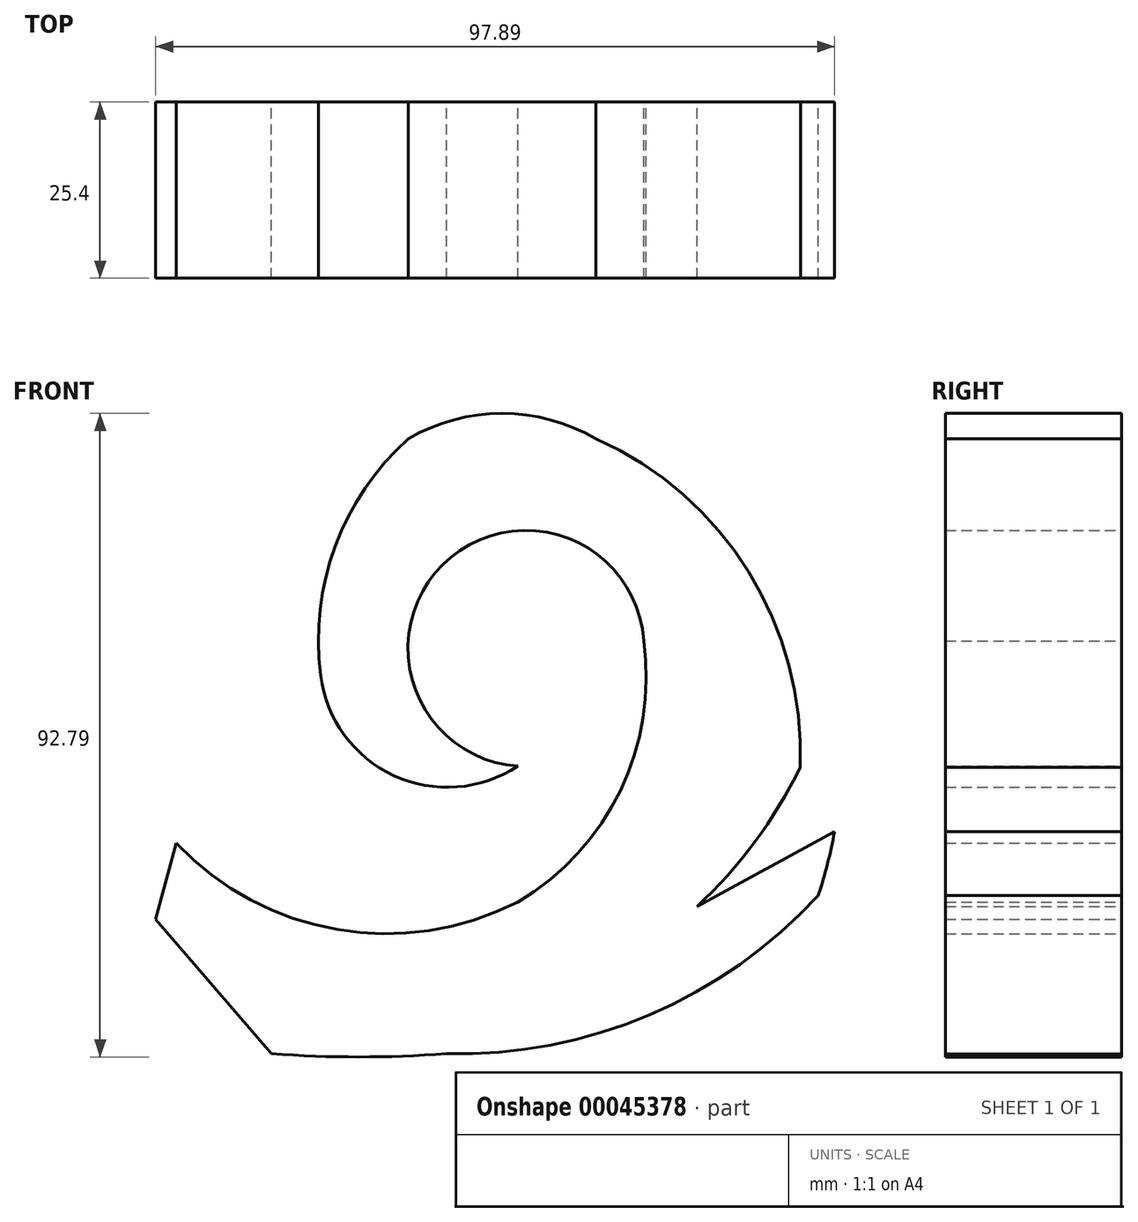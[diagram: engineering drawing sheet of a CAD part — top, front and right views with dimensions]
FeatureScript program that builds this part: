
annotation { "Feature Type Name" : "Feature", "Feature Type Description" : "" }
export const myFeature = defineFeature(function(context is Context, id is Id, definition is map)
    precondition{}
    {
        {
            var Q0;
            Q0=qCreatedBy(makeId("Front.planeOp"),FACE);
            var sketch = newSketch(context, id + "F0", { "sketchPlane" : qUnion([Q0])});
            skArc(sketch, "E0", {"start": v(-28.45, -4.94) * mm, "mid": v(-17.88, -19.42) * mm, "end": v(0, -18.06) * mm});
            skArc(sketch, "E1", {"start": v(18.16, 0) * mm, "mid": v(-10.82, 10.99) * mm, "end": v(0, -18.06) * mm});
            skArc(sketch, "E2", {"start": v(-15.78, 29.16) * mm, "mid": v(-26.32, 13.67) * mm, "end": v(-28.45, -4.94) * mm});
            skArc(sketch, "E3", {"start": v(11.26, 29.16) * mm, "mid": v(-2.26, 32.8) * mm, "end": v(-15.78, 29.16) * mm});
            skArc(sketch, "E4", {"start": v(40.72, -18.26) * mm, "mid": v(33.3, 9.99) * mm, "end": v(11.26, 29.16) * mm});
            skArc(sketch, "E5", {"start": v(0, -37.64) * mm, "mid": v(14.8, -21.57) * mm, "end": v(18.16, 0) * mm});
            skArc(sketch, "E6", {"start": v(10.25, -49.14) * mm, "mid": v(28.02, -36.2) * mm, "end": v(40.72, -18.26) * mm});
            skArc(sketch, "E7", {"start": v(-49.23, -29.16) * mm, "mid": v(-26.03, -41.61) * mm, "end": v(0, -37.64) * mm});
            skArc(sketch, "E8", {"start": v(-35.52, -51.16) * mm, "mid": v(-12.57, -51.62) * mm, "end": v(10.25, -49.14) * mm});
            skLineSegment(sketch, "E9", {"start": v(0, -18.06) * mm, "end": v(0, -23.74) * mm});
            skArc(sketch, "E10", {"start": v(-39.51, -10.04) * mm, "mid": v(-22.53, -24.85) * mm, "end": v(0, -25.45) * mm});
            skArc(sketch, "E11", {"start": v(-34.16, 22.74) * mm, "mid": v(-42.14, 7.21) * mm, "end": v(-39.51, -10.04) * mm});
            skArc(sketch, "E12", {"start": v(2.68, 38.83) * mm, "mid": v(-17.1, 33.9) * mm, "end": v(-34.16, 22.74) * mm});
            skArc(sketch, "E13", {"start": v(40.55, 12.93) * mm, "mid": v(24.95, 30.76) * mm, "end": v(2.68, 38.83) * mm});
            skArc(sketch, "E14", {"start": v(43.33, -36.7) * mm, "mid": v(46.66, -11.62) * mm, "end": v(40.55, 12.93) * mm});
            skArc(sketch, "E15", {"start": v(-10.29, -59.53) * mm, "mid": v(19, -53.93) * mm, "end": v(43.33, -36.7) * mm});
            skArc(sketch, "E16", {"start": v(-35.52, -59.53) * mm, "mid": v(-22.9, -59.99) * mm, "end": v(-10.29, -59.53) * mm});
            skLineSegment(sketch, "E17", {"start": v(-49.23, -29.16) * mm, "end": v(-34.05, -51.28) * mm});
            skLineSegment(sketch, "E18", {"start": v(-34.05, -51.28) * mm, "end": v(-34.05, -59.53) * mm});
            skLineSegment(sketch, "E19", {"start": v(-49.23, -29.16) * mm, "end": v(-52.21, -40.17) * mm});
            skLineSegment(sketch, "E20", {"start": v(-52.21, -40.17) * mm, "end": v(-35.52, -59.53) * mm});
            skLineSegment(sketch, "E21", {"start": v(74.96, -40.28) * mm, "end": v(25.84, -38.3) * mm});
            skLineSegment(sketch, "E22", {"start": v(25.84, -38.3) * mm, "end": v(52.96, -23.52) * mm});
            skLineSegment(sketch, "E23", {"start": v(52.96, -23.52) * mm, "end": v(65.7, -22.46) * mm});
            skSolve(sketch);
        }
        {
            var Q0;
            Q0 = qSketchRegion(id + "F0", true);
            extrude(context, id + "F1", {"entities" : qUnion([Q0]), "depth" : 25.4 * mm});
        }
    });
